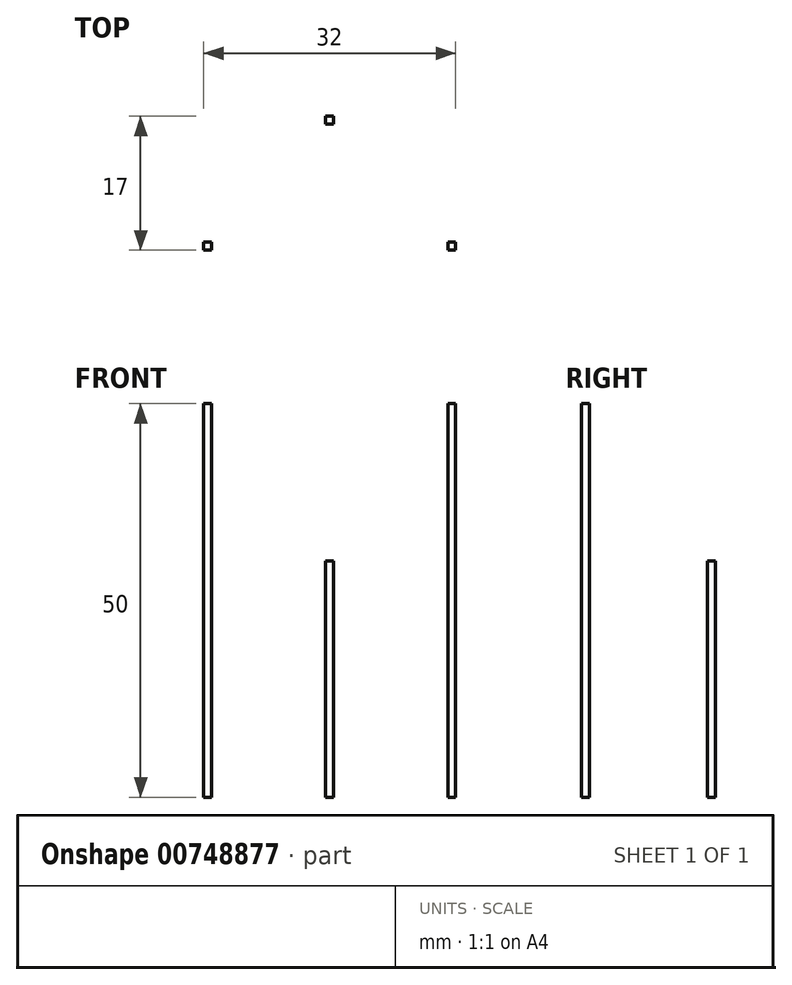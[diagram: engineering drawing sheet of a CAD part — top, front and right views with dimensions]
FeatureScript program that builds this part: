
annotation { "Feature Type Name" : "Feature", "Feature Type Description" : "" }
export const myFeature = defineFeature(function(context is Context, id is Id, definition is map)
    precondition{}
    {
        {
            var Q0;
            Q0=qCreatedBy(makeId("Top.planeOp"),FACE);
            var sketch = newSketch(context, id + "F0", { "sketchPlane" : qUnion([Q0])});
            skLineSegment(sketch, "E0.bottom", {"start": v(-16, 0) * mm, "end": v(-15, 0) * mm});
            skLineSegment(sketch, "E0.top", {"start": v(-16, -1) * mm, "end": v(-15, -1) * mm});
            skLineSegment(sketch, "E0.left", {"start": v(-16, 0) * mm, "end": v(-16, -1) * mm});
            skLineSegment(sketch, "E0.right", {"start": v(-15, 0) * mm, "end": v(-15, -1) * mm});
            skLineSegment(sketch, "E1.bottom", {"start": v(15, 0) * mm, "end": v(16, 0) * mm});
            skLineSegment(sketch, "E1.top", {"start": v(15, -1) * mm, "end": v(16, -1) * mm});
            skLineSegment(sketch, "E1.left", {"start": v(15, 0) * mm, "end": v(15, -1) * mm});
            skLineSegment(sketch, "E1.right", {"start": v(16, 0) * mm, "end": v(16, -1) * mm});
            skLineSegment(sketch, "E2.bottom", {"start": v(0.5, 15) * mm, "end": v(-0.5, 15) * mm});
            skLineSegment(sketch, "E2.top", {"start": v(0.5, 16) * mm, "end": v(-0.5, 16) * mm});
            skLineSegment(sketch, "E2.left", {"start": v(0.5, 15) * mm, "end": v(0.5, 16) * mm});
            skLineSegment(sketch, "E2.right", {"start": v(-0.5, 15) * mm, "end": v(-0.5, 16) * mm});
            skPoint(sketch, "E2.middle", {"position": v(0, 15.5) * mm});
            skSolve(sketch);
        }
        {
            var Q0;
            Q0=makeQuery(id+"F0.imprint","IMPRINT",FACE,{"disambiguationData":[TD([[makeQuery(id+"F0.imprint","IMPRINT",EDGE,{"derivedFrom":sQuery(id+"F0.wireOp",EDGE,"E1.bottom")}),-1.0]])]});
            var Q1;
            Q1=makeQuery(id+"F0.imprint","IMPRINT",FACE,{"disambiguationData":[TD([[makeQuery(id+"F0.imprint","IMPRINT",EDGE,{"derivedFrom":sQuery(id+"F0.wireOp",EDGE,"E0.bottom")}),-1.0]])]});
            extrude(context, id + "F1", {"entities" : qUnion([Q0, Q1]), "depth" : 50 * mm, "offsetDistance" : 25 * mm});
        }
        {
            var Q0;
            Q0=makeQuery(id+"F0.imprint","IMPRINT",FACE,{"disambiguationData":[TD([[makeQuery(id+"F0.imprint","IMPRINT",EDGE,{"derivedFrom":sQuery(id+"F0.wireOp",EDGE,"E2.bottom")}),-1.0]])]});
            extrude(context, id + "F2", {"entities" : qUnion([Q0]), "depth" : 30 * mm, "offsetDistance" : 25 * mm});
        }
    });
